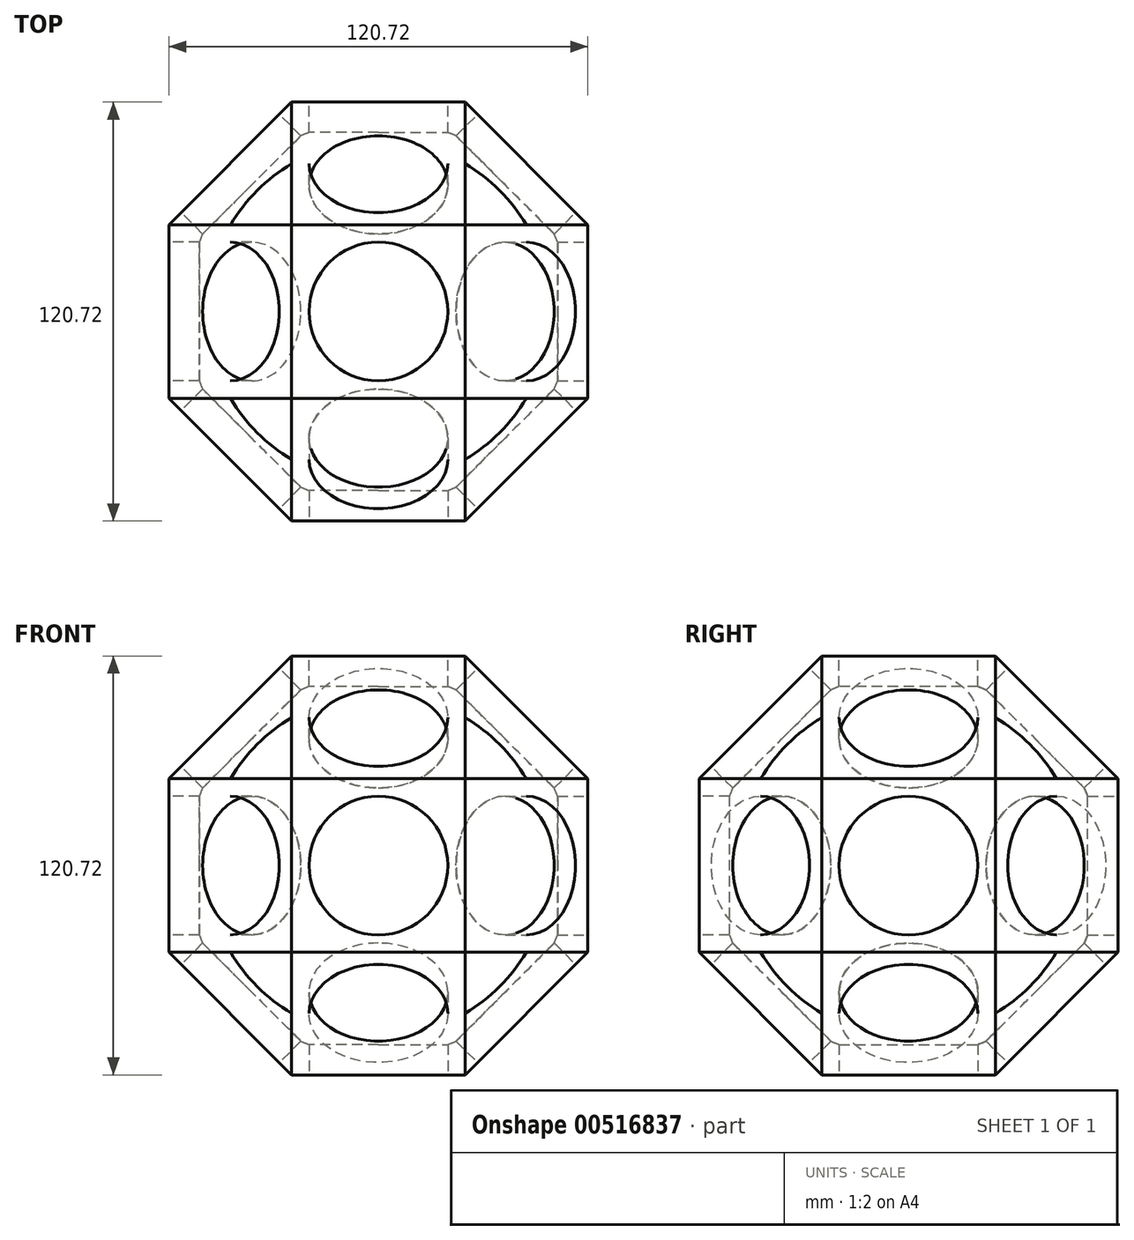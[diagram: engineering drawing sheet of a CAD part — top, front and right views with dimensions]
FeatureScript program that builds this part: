
annotation { "Feature Type Name" : "Feature", "Feature Type Description" : "" }
export const myFeature = defineFeature(function(context is Context, id is Id, definition is map)
    precondition{}
    {
        {
            var Q0;
            Q0=qCreatedBy(makeId("Front.planeOp"),FACE);
            var sketch = newSketch(context, id + "F0", { "sketchPlane" : qUnion([Q0])});
            skLineSegment(sketch, "E0", {"start": v(0, 0) * mm, "end": v(0, -5) * mm});
            skLineSegment(sketch, "E1", {"start": v(0, -5) * mm, "end": v(0, -25) * mm});
            skLineSegment(sketch, "E2", {"start": v(0, -25) * mm, "end": v(60.36, -25) * mm});
            skLineSegment(sketch, "E3", {"start": v(60.36, -25) * mm, "end": v(60.36, 0) * mm});
            skLineSegment(sketch, "E4", {"start": v(60.36, 0) * mm, "end": v(60.36, 20) * mm});
            skLineSegment(sketch, "E5", {"start": v(60.36, 20) * mm, "end": v(60.36, 25) * mm});
            skLineSegment(sketch, "E6", {"start": v(60.36, 25) * mm, "end": v(0, 25) * mm});
            skLineSegment(sketch, "E7", {"start": v(0, 25) * mm, "end": v(0, 5) * mm});
            skLineSegment(sketch, "E8", {"start": v(0, 5) * mm, "end": v(0, 0) * mm});
            skLineSegment(sketch, "E9", {"start": v(0, 0) * mm, "end": v(25, 0) * mm, "construction": true});
            skLineSegment(sketch, "E10", {"start": v(25, 0) * mm, "end": v(25, -60.36) * mm, "construction": true});
            skLineSegment(sketch, "E11", {"start": v(25, -60.36) * mm, "end": v(42.68, -42.68) * mm, "construction": true});
            skLineSegment(sketch, "E12", {"start": v(42.68, -42.68) * mm, "end": v(60.36, -25) * mm, "construction": true});
            skLineSegment(sketch, "E13", {"start": v(42.68, -42.68) * mm, "end": v(39.14, -39.14) * mm, "construction": true});
            skCircle(sketch, "E14", {"center": v(0, 0) * mm, "radius": 55.36 * mm});
            skLineSegment(sketch, "E15", {"start": v(0, 25) * mm, "end": v(0, 55.36) * mm});
            skLineSegment(sketch, "E16", {"start": v(0, -25) * mm, "end": v(0, -55.36) * mm});
            skSolve(sketch);
        }
        {
            var Q0;
            Q0=makeQuery(id+"F0.imprint","IMPRINT",FACE,{"disambiguationData":[TD([[makeQuery(id+"F0.imprint","IMPRINT",EDGE,{"derivedFrom":sQuery(id+"F0.wireOp",EDGE,"E4")}),1.0]])]});
            var Q1;
            Q1=makeQuery(id+"F0.imprint","IMPRINT",FACE,{"disambiguationData":[TD([[makeQuery(id+"F0.imprint","IMPRINT",EDGE,{"derivedFrom":sQuery(id+"F0.wireOp",EDGE,"E5")}),1.0]])]});
            var Q2;
            Q2=makeQuery(id+"F0.imprint","IMPRINT",FACE,{"disambiguationData":[TD([[makeQuery(id+"F0.imprint","IMPRINT",EDGE,{"derivedFrom":sQuery(id+"F0.wireOp",EDGE,"E0")}),1.0]])]});
            extrude(context, id + "F1", {"entities" : qUnion([Q0, Q1, Q2]), "depth" : 25 * mm, "offsetDistance" : 25 * mm, "hasSecondDirection" : true, "secondDirectionOppositeDirection" : true, "secondDirectionDepth" : 25 * mm});
        }
        {
            var Q0;
            Q0=makeQuery(id+"F1.opExtrude","SWEPT_FACE",FACE,{"disambiguationData":[OSD([sQuery(id+"F0.wireOp",EDGE,"E3"),sQuery(id+"F0.wireOp",EDGE,"E4"),sQuery(id+"F0.wireOp",EDGE,"E5")])]});
            var sketch = newSketch(context, id + "F2", { "sketchPlane" : qUnion([Q0])});
            skCircle(sketch, "E17", {"center": v(0, 0) * mm, "radius": 20 * mm});
            skLineSegment(sketch, "E18", {"start": v(0, 0) * mm, "end": v(0, 20) * mm, "construction": true});
            skSolve(sketch);
        }
        {
            var Q0;
            Q0=makeQuery(id+"F2.imprint","IMPRINT",FACE,{"disambiguationData":[TD([[makeQuery(id+"F2.imprint","IMPRINT",EDGE,{"derivedFrom":sQuery(id+"F2.wireOp",EDGE,"E17")}),1.0]])]});
            extrude(context, id + "F3", {"entities" : qUnion([Q0]), "operationType" : NewBodyOperationType.REMOVE, "oppositeDirection" : true, "depth" : 2 * mm, "offsetDistance" : 25 * mm});
        }
        {
            var Q0;
            Q0=makeQuery(id+"F1.opExtrude","SWEPT_BODY",BODY,{"disambiguationData":[OSD([sQuery(id+"F0.wireOp",EDGE,"E0"),sQuery(id+"F0.wireOp",EDGE,"E1"),sQuery(id+"F0.wireOp",EDGE,"E2"),sQuery(id+"F0.wireOp",EDGE,"E3"),sQuery(id+"F0.wireOp",EDGE,"E4"),sQuery(id+"F0.wireOp",EDGE,"E5"),sQuery(id+"F0.wireOp",EDGE,"E6"),sQuery(id+"F0.wireOp",EDGE,"E7"),sQuery(id+"F0.wireOp",EDGE,"E8")])]});
            var Q1;
            Q1=sQuery(id+"F0.wireOp",EDGE,"E1");
            circularPattern(context, id + "F4", {"operationType" : NewBodyOperationType.ADD, "entities" : qUnion([Q0]), "axis" : qUnion([Q1]), "angle" : 180 * degree, "instanceCount" : 5, "equalSpace" : true});
        }
        {
            var Q0;
            Q0=makeQuery(id+"F1.opExtrude","SWEPT_BODY",BODY,{"disambiguationData":[OSD([sQuery(id+"F0.wireOp",EDGE,"E0"),sQuery(id+"F0.wireOp",EDGE,"E1"),sQuery(id+"F0.wireOp",EDGE,"E2"),sQuery(id+"F0.wireOp",EDGE,"E3"),sQuery(id+"F0.wireOp",EDGE,"E4"),sQuery(id+"F0.wireOp",EDGE,"E5"),sQuery(id+"F0.wireOp",EDGE,"E6"),sQuery(id+"F0.wireOp",EDGE,"E7"),sQuery(id+"F0.wireOp",EDGE,"E8")])]});
            var Q1;
            Q1=sQuery(id+"F0.wireOp",EDGE,"E9");
            circularPattern(context, id + "F5", {"operationType" : NewBodyOperationType.ADD, "entities" : qUnion([Q0]), "axis" : qUnion([Q1]), "angle" : 360 * degree, "instanceCount" : 4, "equalSpace" : true});
        }
        {
            var Q0;
            Q0=makeQuery(id+"F1.opExtrude","SWEPT_BODY",BODY,{"disambiguationData":[OSD([sQuery(id+"F0.wireOp",EDGE,"E0"),sQuery(id+"F0.wireOp",EDGE,"E1"),sQuery(id+"F0.wireOp",EDGE,"E2"),sQuery(id+"F0.wireOp",EDGE,"E3"),sQuery(id+"F0.wireOp",EDGE,"E4"),sQuery(id+"F0.wireOp",EDGE,"E5"),sQuery(id+"F0.wireOp",EDGE,"E6"),sQuery(id+"F0.wireOp",EDGE,"E7"),sQuery(id+"F0.wireOp",EDGE,"E8")])]});
            var Q1;
            Q1=sQuery(id+"F0.wireOp",EDGE,"E7");
            circularPattern(context, id + "F6", {"operationType" : NewBodyOperationType.ADD, "entities" : qUnion([Q0]), "axis" : qUnion([Q1]), "angle" : 90 * degree, "instanceCount" : 2, "equalSpace" : true});
        }
        {
            var Q0;
            Q0=makeQuery(id+"F0.imprint","IMPRINT",FACE,{"disambiguationData":[TD([[makeQuery(id+"F0.imprint","IMPRINT",EDGE,{"derivedFrom":sQuery(id+"F0.wireOp",EDGE,"E0")}),-1.0]])]});
            var Q1;
            Q1=sQuery(id+"F0.wireOp",EDGE,"E1");
            revolve(context, id + "F7", {"operationType" : NewBodyOperationType.REMOVE, "entities" : qUnion([Q0]), "axis" : qUnion([Q1]), "revolveType" : RevolveType.FULL, "oppositeDirection" : true});
        }
        {
            var Q0;
            Q0=makeQuery(id+"F5.opPattern","COPY",FACE,{"derivedFrom":makeQuery(id+"F4.opPattern","COPY",FACE,{"derivedFrom":makeQuery(id+"F3.boolean.opBoolean","COPY",FACE,{"derivedFrom":makeQuery(id+"F3.opExtrude","CAP_FACE",FACE,{"disambiguationData":[OSD([sQuery(id+"F2.wireOp",EDGE,"E17")])],"isStart":false})}),"instanceName":"2"}),"instanceName":"3"});
            extrude(context, id + "F8", {"entities" : qUnion([Q0]), "operationType" : NewBodyOperationType.REMOVE, "endBound" : BoundingType.THROUGH_ALL, "oppositeDirection" : true, "depth" : 200 * mm, "offsetDistance" : 25 * mm});
        }
        {
            var Q0;
            Q0=makeQuery(id+"F6.opPattern","COPY",FACE,{"derivedFrom":makeQuery(id+"F5.opPattern","COPY",FACE,{"derivedFrom":makeQuery(id+"F4.opPattern","COPY",FACE,{"derivedFrom":makeQuery(id+"F3.boolean.opBoolean","COPY",FACE,{"derivedFrom":makeQuery(id+"F3.opExtrude","CAP_FACE",FACE,{"disambiguationData":[OSD([sQuery(id+"F2.wireOp",EDGE,"E17")])],"isStart":false})}),"instanceName":"3"}),"instanceName":"3"}),"instanceName":"1"});
            extrude(context, id + "F9", {"entities" : qUnion([Q0]), "operationType" : NewBodyOperationType.REMOVE, "endBound" : BoundingType.THROUGH_ALL, "oppositeDirection" : true, "depth" : 25 * mm, "offsetDistance" : 25 * mm});
        }
        {
            var Q0;
            Q0=makeQuery(id+"F5.opPattern","COPY",FACE,{"derivedFrom":makeQuery(id+"F4.opPattern","COPY",FACE,{"derivedFrom":makeQuery(id+"F3.boolean.opBoolean","COPY",FACE,{"derivedFrom":makeQuery(id+"F3.opExtrude","CAP_FACE",FACE,{"disambiguationData":[OSD([sQuery(id+"F2.wireOp",EDGE,"E17")])],"isStart":false})}),"instanceName":"2"}),"instanceName":"2"});
            extrude(context, id + "F10", {"entities" : qUnion([Q0]), "operationType" : NewBodyOperationType.REMOVE, "endBound" : BoundingType.THROUGH_ALL, "oppositeDirection" : true, "depth" : 25 * mm, "offsetDistance" : 25 * mm});
        }
        {
            var Q0;
            Q0=makeQuery(id+"F6.opPattern","COPY",FACE,{"derivedFrom":makeQuery(id+"F5.opPattern","COPY",FACE,{"derivedFrom":makeQuery(id+"F4.opPattern","COPY",FACE,{"derivedFrom":makeQuery(id+"F3.boolean.opBoolean","COPY",FACE,{"derivedFrom":makeQuery(id+"F3.opExtrude","CAP_FACE",FACE,{"disambiguationData":[OSD([sQuery(id+"F2.wireOp",EDGE,"E17")])],"isStart":false})}),"instanceName":"3"}),"instanceName":"1"}),"instanceName":"1"});
            extrude(context, id + "F11", {"entities" : qUnion([Q0]), "operationType" : NewBodyOperationType.REMOVE, "endBound" : BoundingType.THROUGH_ALL, "oppositeDirection" : true, "depth" : 25 * mm, "offsetDistance" : 25 * mm});
        }
        {
            var Q0;
            Q0=makeQuery(id+"F5.opPattern","COPY",FACE,{"derivedFrom":makeQuery(id+"F4.opPattern","COPY",FACE,{"derivedFrom":makeQuery(id+"F3.boolean.opBoolean","COPY",FACE,{"derivedFrom":makeQuery(id+"F3.opExtrude","CAP_FACE",FACE,{"disambiguationData":[OSD([sQuery(id+"F2.wireOp",EDGE,"E17")])],"isStart":false})}),"instanceName":"3"}),"instanceName":"2"});
            extrude(context, id + "F12", {"entities" : qUnion([Q0]), "operationType" : NewBodyOperationType.REMOVE, "endBound" : BoundingType.THROUGH_ALL, "oppositeDirection" : true, "depth" : 25 * mm, "offsetDistance" : 25 * mm});
        }
        {
            var Q0;
            Q0=makeQuery(id+"F4.opPattern","COPY",FACE,{"derivedFrom":makeQuery(id+"F3.boolean.opBoolean","COPY",FACE,{"derivedFrom":makeQuery(id+"F3.opExtrude","CAP_FACE",FACE,{"disambiguationData":[OSD([sQuery(id+"F2.wireOp",EDGE,"E17")])],"isStart":false})}),"instanceName":"4"});
            extrude(context, id + "F13", {"entities" : qUnion([Q0]), "operationType" : NewBodyOperationType.REMOVE, "endBound" : BoundingType.THROUGH_ALL, "oppositeDirection" : true, "depth" : 25 * mm, "offsetDistance" : 25 * mm});
        }
        {
            var Q0;
            Q0=makeQuery(id+"F5.opPattern","COPY",FACE,{"derivedFrom":makeQuery(id+"F4.opPattern","COPY",FACE,{"derivedFrom":makeQuery(id+"F3.boolean.opBoolean","COPY",FACE,{"derivedFrom":makeQuery(id+"F3.opExtrude","CAP_FACE",FACE,{"disambiguationData":[OSD([sQuery(id+"F2.wireOp",EDGE,"E17")])],"isStart":false})}),"instanceName":"3"}),"instanceName":"3"});
            extrude(context, id + "F14", {"entities" : qUnion([Q0]), "operationType" : NewBodyOperationType.REMOVE, "endBound" : BoundingType.THROUGH_ALL, "oppositeDirection" : true, "depth" : 25 * mm, "offsetDistance" : 25 * mm});
        }
        {
            var Q0;
            Q0=makeQuery(id+"F5.opPattern","COPY",FACE,{"derivedFrom":makeQuery(id+"F4.opPattern","COPY",FACE,{"derivedFrom":makeQuery(id+"F3.boolean.opBoolean","COPY",FACE,{"derivedFrom":makeQuery(id+"F3.opExtrude","CAP_FACE",FACE,{"disambiguationData":[OSD([sQuery(id+"F2.wireOp",EDGE,"E17")])],"isStart":false})}),"instanceName":"3"}),"instanceName":"1"});
            extrude(context, id + "F15", {"entities" : qUnion([Q0]), "operationType" : NewBodyOperationType.REMOVE, "endBound" : BoundingType.THROUGH_ALL, "oppositeDirection" : true, "depth" : 25 * mm, "offsetDistance" : 25 * mm});
        }
        {
            var Q0;
            Q0=makeQuery(id+"F4.opPattern","COPY",FACE,{"derivedFrom":makeQuery(id+"F3.boolean.opBoolean","COPY",FACE,{"derivedFrom":makeQuery(id+"F3.opExtrude","CAP_FACE",FACE,{"disambiguationData":[OSD([sQuery(id+"F2.wireOp",EDGE,"E17")])],"isStart":false})}),"instanceName":"3"});
            extrude(context, id + "F16", {"entities" : qUnion([Q0]), "operationType" : NewBodyOperationType.REMOVE, "endBound" : BoundingType.THROUGH_ALL, "oppositeDirection" : true, "depth" : 25 * mm, "offsetDistance" : 25 * mm});
        }
    });
